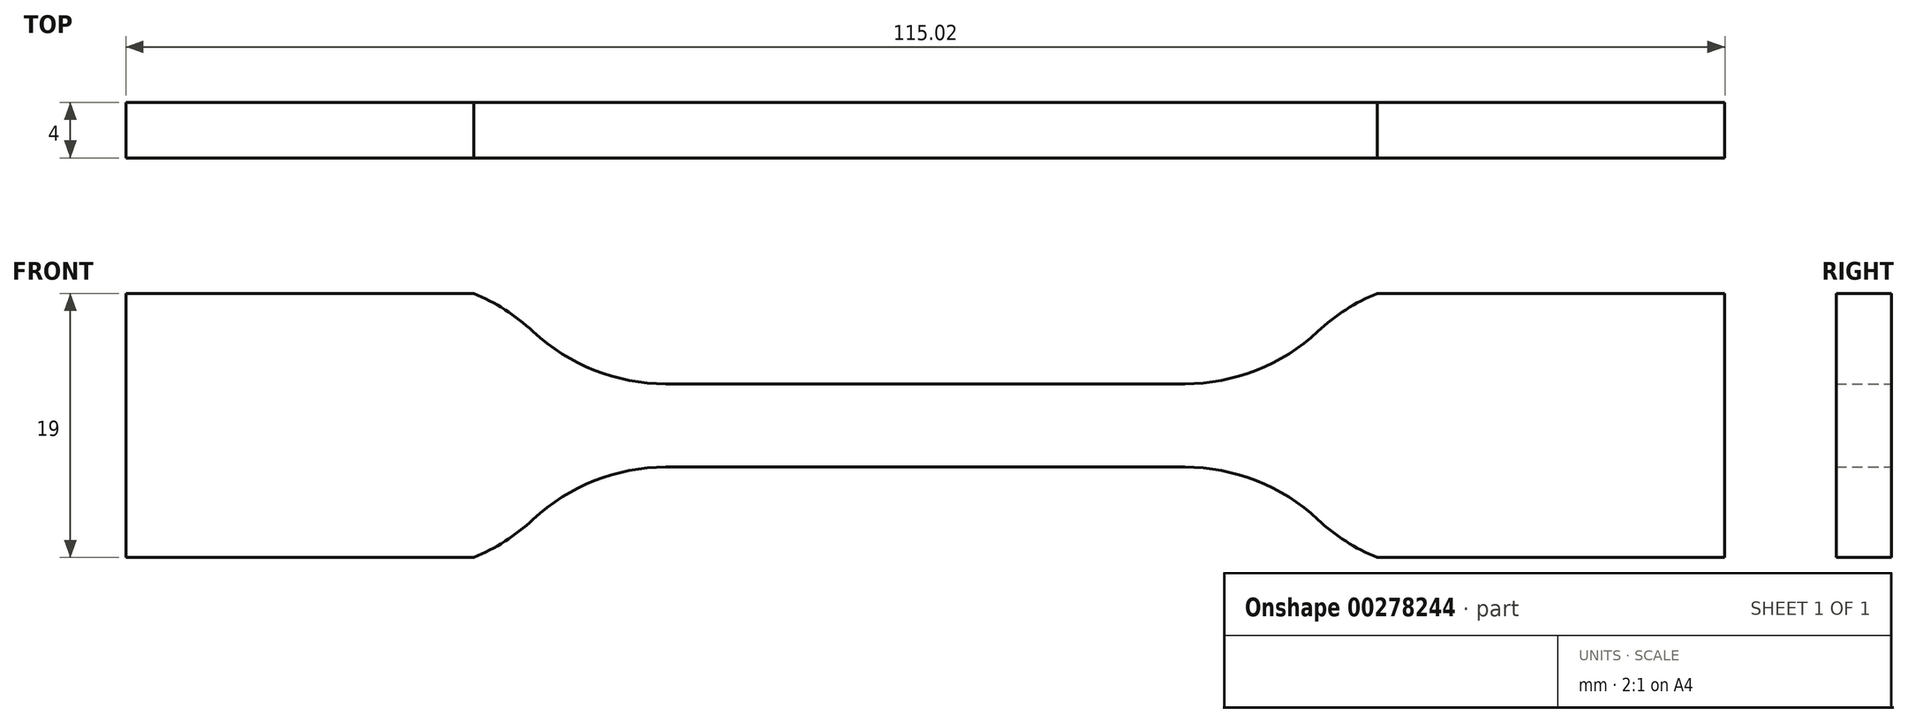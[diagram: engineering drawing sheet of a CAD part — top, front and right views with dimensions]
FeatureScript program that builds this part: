
annotation { "Feature Type Name" : "Feature", "Feature Type Description" : "" }
export const myFeature = defineFeature(function(context is Context, id is Id, definition is map)
    precondition{}
    {
        {
            var Q0;
            Q0=qCreatedBy(makeId("Front.planeOp"),FACE);
            var sketch = newSketch(context, id + "F0", { "sketchPlane" : qUnion([Q0])});
            skLineSegment(sketch, "E0", {"start": v(0, 3) * mm, "end": v(18.67, 3) * mm});
            skArc(sketch, "E1", {"start": v(32.5, 9.5) * mm, "mid": v(30.24, 8.33) * mm, "end": v(28.23, 6.77) * mm});
            skLineSegment(sketch, "E2", {"start": v(32.5, 9.5) * mm, "end": v(57.5, 9.5) * mm});
            skLineSegment(sketch, "E3", {"start": v(57.5, 9.5) * mm, "end": v(57.5, 0) * mm});
            skLineSegment(sketch, "E4.MirrorCS", {"start": v(0, -3) * mm, "end": v(18.67, -3) * mm});
            skLineSegment(sketch, "E5.MirrorCS", {"start": v(32.5, -9.5) * mm, "end": v(57.5, -9.5) * mm});
            skLineSegment(sketch, "E6.MirrorCS", {"start": v(57.5, -9.5) * mm, "end": v(57.5, 0) * mm});
            skArc(sketch, "E7.MirrorCS", {"start": v(32.5, -9.5) * mm, "mid": v(30.24, -8.33) * mm, "end": v(28.23, -6.77) * mm});
            skArc(sketch, "E8.MirrorCS", {"start": v(-32.5, 9.5) * mm, "mid": v(-30.24, 8.33) * mm, "end": v(-28.23, 6.77) * mm});
            skLineSegment(sketch, "E9.MirrorCS", {"start": v(-57.5, -9.5) * mm, "end": v(-57.5, 0) * mm});
            skLineSegment(sketch, "E10.MirrorCS", {"start": v(-32.5, 9.5) * mm, "end": v(-57.5, 9.5) * mm});
            skLineSegment(sketch, "E11.MirrorCS", {"start": v(0, 3) * mm, "end": v(-18.67, 3) * mm});
            skLineSegment(sketch, "E12.MirrorCS", {"start": v(-57.5, 9.5) * mm, "end": v(-57.5, 0) * mm});
            skArc(sketch, "E13.MirrorCS", {"start": v(-32.5, -9.5) * mm, "mid": v(-30.24, -8.33) * mm, "end": v(-28.23, -6.77) * mm});
            skLineSegment(sketch, "E14.MirrorCS", {"start": v(-32.5, -9.5) * mm, "end": v(-57.5, -9.5) * mm});
            skLineSegment(sketch, "E15.MirrorCS", {"start": v(0, -3) * mm, "end": v(-18.67, -3) * mm});
            skPoint(sketch, "E16.visualSharp", {"position": v(-50.2, 3) * mm});
            skArc(sketch, "E16.filletArc", {"start": v(-28.23, 6.77) * mm, "mid": v(-23.81, 3.97) * mm, "end": v(-18.67, 3) * mm});
            skPoint(sketch, "E17.visualSharp", {"position": v(-50.2, -3) * mm});
            skArc(sketch, "E17.filletArc", {"start": v(-18.67, -3) * mm, "mid": v(-23.81, -3.97) * mm, "end": v(-28.23, -6.77) * mm});
            skPoint(sketch, "E18.visualSharp", {"position": v(50.2, 3) * mm});
            skArc(sketch, "E18.filletArc", {"start": v(18.67, 3) * mm, "mid": v(23.81, 3.97) * mm, "end": v(28.23, 6.77) * mm});
            skPoint(sketch, "E19.visualSharp", {"position": v(50.2, -3) * mm});
            skArc(sketch, "E19.filletArc", {"start": v(28.23, -6.77) * mm, "mid": v(23.81, -3.97) * mm, "end": v(18.67, -3) * mm});
            skSolve(sketch);
        }
        {
            var Q0;
            Q0 = qSketchRegion(id + "F0", true);
            extrude(context, id + "F1", {"entities" : qUnion([Q0]), "endBound" : BoundingType.SYMMETRIC, "depth" : 4 * mm});
        }
    });
